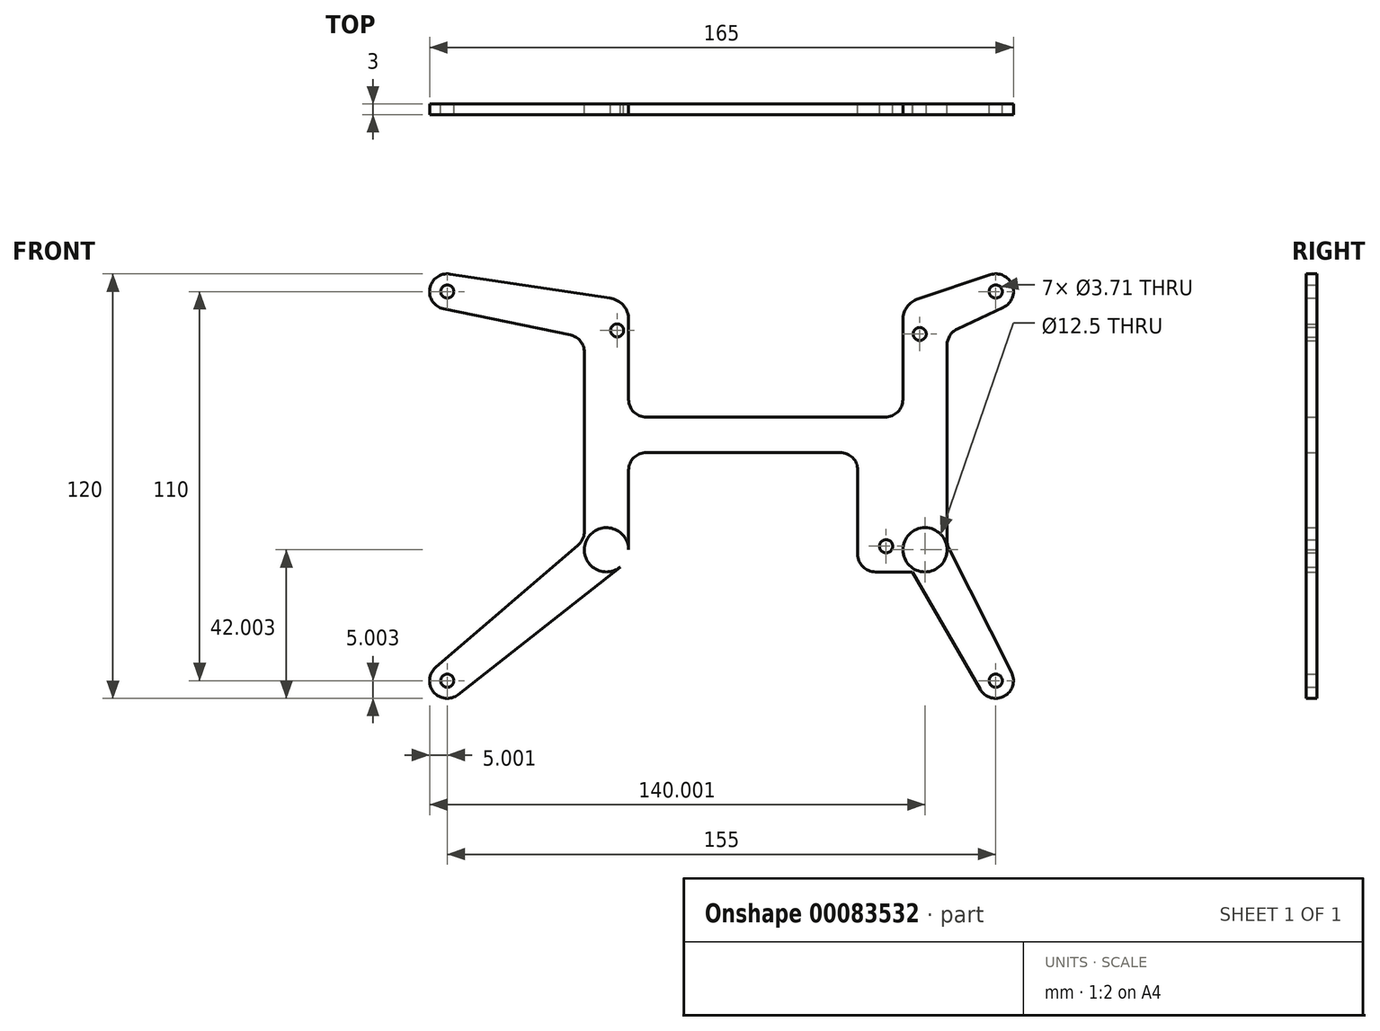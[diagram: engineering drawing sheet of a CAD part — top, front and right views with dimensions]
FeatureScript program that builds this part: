
annotation { "Feature Type Name" : "Feature", "Feature Type Description" : "" }
export const myFeature = defineFeature(function(context is Context, id is Id, definition is map)
    precondition{}
    {
        {
            var Q0;
            Q0=qCreatedBy(makeId("Front.planeOp"),FACE);
            var sketch = newSketch(context, id + "F0", { "sketchPlane" : qUnion([Q0])});
            skLineSegment(sketch, "E0.bottom", {"start": v(-70.99, 55.43) * mm, "end": v(84.01, 55.43) * mm});
            skLineSegment(sketch, "E0.top", {"start": v(-70.99, -54.57) * mm, "end": v(84.01, -54.57) * mm});
            skLineSegment(sketch, "E0.left", {"start": v(-70.99, 55.43) * mm, "end": v(-70.99, -54.57) * mm});
            skLineSegment(sketch, "E0.right", {"start": v(84.01, 55.43) * mm, "end": v(84.01, -54.57) * mm});
            skCircle(sketch, "E1", {"center": v(-70.99, 55.43) * mm, "radius": 5 * mm});
            skCircle(sketch, "E2", {"center": v(84.01, 55.43) * mm, "radius": 5 * mm});
            skCircle(sketch, "E3", {"center": v(84.01, -54.57) * mm, "radius": 5 * mm});
            skCircle(sketch, "E4", {"center": v(-70.99, -54.57) * mm, "radius": 5 * mm});
            skLineSegment(sketch, "E5", {"start": v(84.01, 55.43) * mm, "end": v(84.01, 47.43) * mm});
            skLineSegment(sketch, "E6", {"start": v(84.01, 47.43) * mm, "end": v(64.01, 47.43) * mm});
            skCircle(sketch, "E7", {"center": v(64.01, 47.43) * mm, "radius": 6.25 * mm});
            skLineSegment(sketch, "E8", {"start": v(64.01, 47.43) * mm, "end": v(64.01, -17.57) * mm});
            skCircle(sketch, "E9", {"center": v(64.01, -17.57) * mm, "radius": 6.25 * mm});
            skLineSegment(sketch, "E10", {"start": v(64.01, 47.43) * mm, "end": v(-19.74, 47.43) * mm});
            skLineSegment(sketch, "E11", {"start": v(-25.99, 47.43) * mm, "end": v(-25.99, -17.57) * mm});
            skLineSegment(sketch, "E12", {"start": v(-25.99, -17.57) * mm, "end": v(64.01, -17.57) * mm});
            skCircle(sketch, "E13", {"center": v(-25.99, 47.43) * mm, "radius": 6.25 * mm});
            skCircle(sketch, "E14", {"center": v(-25.99, -17.57) * mm, "radius": 6.25 * mm});
            skLineSegment(sketch, "E15", {"start": v(-70.25, 60.38) * mm, "end": v(-25.06, 53.61) * mm});
            skLineSegment(sketch, "E16", {"start": v(-36.23, 43.16) * mm, "end": v(-72, 50.54) * mm});
            skLineSegment(sketch, "E17", {"start": v(-74.25, -50.77) * mm, "end": v(-33.98, -16.2) * mm});
            skLineSegment(sketch, "E18", {"start": v(82.43, 60.18) * mm, "end": v(62.03, 53.36) * mm});
            skLineSegment(sketch, "E19", {"start": v(86.13, 50.9) * mm, "end": v(73.14, 44.81) * mm});
            skLineSegment(sketch, "E20", {"start": v(79.68, -57.07) * mm, "end": v(58.6, -20.7) * mm});
            skLineSegment(sketch, "E21", {"start": v(88.48, -52.32) * mm, "end": v(70.8, -17.14) * mm});
            skLineSegment(sketch, "E22", {"start": v(50.01, -23.82) * mm, "end": v(66.05, -23.82) * mm});
            skLineSegment(sketch, "E23", {"start": v(-32.24, 38.27) * mm, "end": v(-32.24, -12.4) * mm});
            skLineSegment(sketch, "E24", {"start": v(-25.99, 53.68) * mm, "end": v(-25.52, 53.68) * mm});
            skLineSegment(sketch, "E25", {"start": v(70.26, -14.9) * mm, "end": v(70.26, 40.28) * mm});
            skLineSegment(sketch, "E26", {"start": v(-19.74, 47.43) * mm, "end": v(-19.74, 24.93) * mm});
            skLineSegment(sketch, "E27", {"start": v(57.76, 47.43) * mm, "end": v(57.76, 24.93) * mm});
            skLineSegment(sketch, "E28", {"start": v(-25.99, 47.43) * mm, "end": v(-22.99, 47.43) * mm});
            skLineSegment(sketch, "E29", {"start": v(-22.99, 47.43) * mm, "end": v(-22.99, 44.43) * mm});
            skCircle(sketch, "E30", {"center": v(-22.99, 44.43) * mm, "radius": 1.85 * mm});
            skLineSegment(sketch, "E31", {"start": v(-25.99, -17.57) * mm, "end": v(-23.99, -17.57) * mm});
            skLineSegment(sketch, "E32", {"start": v(-23.99, -17.57) * mm, "end": v(-23.99, -15.57) * mm});
            skCircle(sketch, "E33", {"center": v(-23.99, -15.57) * mm, "radius": 1.85 * mm});
            skLineSegment(sketch, "E34", {"start": v(64.01, -17.57) * mm, "end": v(53.01, -17.57) * mm});
            skLineSegment(sketch, "E35", {"start": v(53.01, -17.57) * mm, "end": v(53.01, -16.57) * mm});
            skCircle(sketch, "E36", {"center": v(53.01, -16.57) * mm, "radius": 1.85 * mm});
            skLineSegment(sketch, "E37", {"start": v(64.01, 47.43) * mm, "end": v(64.01, 43.43) * mm});
            skLineSegment(sketch, "E38", {"start": v(64.01, 43.43) * mm, "end": v(62.51, 43.43) * mm});
            skCircle(sketch, "E39", {"center": v(62.51, 43.43) * mm, "radius": 1.85 * mm});
            skLineSegment(sketch, "E40.0", {"start": v(-14.74, 9.93) * mm, "end": v(40.01, 9.93) * mm});
            skLineSegment(sketch, "E41.0", {"start": v(-14.74, 19.93) * mm, "end": v(52.76, 19.93) * mm});
            skLineSegment(sketch, "E42.trimOffspring", {"start": v(-19.74, 4.93) * mm, "end": v(-19.74, -17.57) * mm});
            skPoint(sketch, "E43.visualSharp", {"position": v(-19.74, 19.93) * mm});
            skArc(sketch, "E43.filletArc", {"start": v(-19.74, 24.93) * mm, "mid": v(-18.27, 21.4) * mm, "end": v(-14.74, 19.93) * mm});
            skPoint(sketch, "E44.visualSharp", {"position": v(-19.74, 9.93) * mm});
            skArc(sketch, "E44.filletArc", {"start": v(-14.74, 9.93) * mm, "mid": v(-18.27, 8.47) * mm, "end": v(-19.74, 4.93) * mm});
            skPoint(sketch, "E45.visualSharp", {"position": v(57.76, 19.93) * mm});
            skArc(sketch, "E45.filletArc", {"start": v(52.76, 19.93) * mm, "mid": v(56.3, 21.4) * mm, "end": v(57.76, 24.93) * mm});
            skLineSegment(sketch, "E46", {"start": v(45.01, 4.93) * mm, "end": v(45.01, -18.82) * mm});
            skArc(sketch, "E47.filletArc", {"start": v(-32.24, 38.27) * mm, "mid": v(-33.36, 41.42) * mm, "end": v(-36.23, 43.16) * mm});
            skArc(sketch, "E48.filletArc", {"start": v(-33.98, -16.2) * mm, "mid": v(-32.7, -14.49) * mm, "end": v(-32.24, -12.4) * mm});
            skArc(sketch, "E49.filletArc", {"start": v(45.01, 4.93) * mm, "mid": v(43.55, 8.47) * mm, "end": v(40.01, 9.93) * mm});
            skArc(sketch, "E50.filletArc", {"start": v(45.01, -18.82) * mm, "mid": v(46.48, -22.35) * mm, "end": v(50.01, -23.82) * mm});
            skLineSegment(sketch, "E51", {"start": v(-67.9, -58.5) * mm, "end": v(-22.12, -22.48) * mm});
            skLineSegment(sketch, "E52.trimOffspring", {"start": v(63, 53.68) * mm, "end": v(64.01, 53.68) * mm});
            skCircle(sketch, "E53", {"center": v(-70.99, 55.43) * mm, "radius": 1.85 * mm});
            skCircle(sketch, "E54", {"center": v(-70.99, -54.57) * mm, "radius": 1.85 * mm});
            skCircle(sketch, "E55", {"center": v(84.01, -54.57) * mm, "radius": 1.85 * mm});
            skCircle(sketch, "E56", {"center": v(84.01, 55.43) * mm, "radius": 1.85 * mm});
            skArc(sketch, "E57.filletArc", {"start": v(73.14, 44.81) * mm, "mid": v(71.04, 42.97) * mm, "end": v(70.26, 40.28) * mm});
            skArc(sketch, "E58.filletArc", {"start": v(70.26, -14.9) * mm, "mid": v(70.4, -16.05) * mm, "end": v(70.8, -17.14) * mm});
            skSolve(sketch);
        }
        {
            var Q0;
            Q0=makeQuery(id+"F0.imprint","IMPRINT",FACE,{"disambiguationData":[TD([[makeQuery(id+"F0.imprint","IMPRINT",EDGE,{"derivedFrom":sQuery(id+"F0.wireOp",EDGE,"E23")}),1.0]])]});
            var Q1;
            {var subQ0=sQuery(id+"F0.wireOp",EDGE,"E15");var subQ1=sQuery(id+"F0.wireOp",EDGE,"E0.bottom");var subQ2=makeQuery(id+"F0.imprint","INTERSECT",VERTEX,{"derivedFrom":[subQ1,subQ0]});Q1=makeQuery(id+"F0.imprint","IMPRINT",FACE,{"disambiguationData":[TD([[makeQuery(id+"F0.imprint","IMPRINT",EDGE,{"disambiguationData":[TD([[subQ2,1.0]])],"derivedFrom":subQ1}),1.0]])]});}
            var Q2;
            Q2=makeQuery(id+"F0.imprint","IMPRINT",FACE,{"disambiguationData":[TD([[makeQuery(id+"F0.imprint","IMPRINT",EDGE,{"derivedFrom":sQuery(id+"F0.wireOp",EDGE,"E30")}),-1.0]])]});
            var Q3;
            {var subQ7=sQuery(id+"F0.wireOp",EDGE,"E26");Q3=makeQuery(id+"F0.imprint","IMPRINT",FACE,{"disambiguationData":[TD([[makeQuery(id+"F0.imprint","IMPRINT",EDGE,{"derivedFrom":subQ7}),-1.0]])]});}
            var Q4;
            {var subQ4=sQuery(id+"F0.wireOp",EDGE,"E31");Q4=makeQuery(id+"F0.imprint","IMPRINT",FACE,{"disambiguationData":[TD([[makeQuery(id+"F0.imprint","IMPRINT",EDGE,{"derivedFrom":subQ4}),-1.0]])]});}
            var Q5;
            {var subQ0=sQuery(id+"F0.wireOp",EDGE,"E31");Q5=makeQuery(id+"F0.imprint","IMPRINT",FACE,{"disambiguationData":[TD([[makeQuery(id+"F0.imprint","IMPRINT",EDGE,{"derivedFrom":subQ0}),1.0]])]});}
            var Q6;
            {var subQ0=sQuery(id+"F0.wireOp",EDGE,"E51");var subQ1=sQuery(id+"F0.wireOp",EDGE,"E0.top");var subQ2=makeQuery(id+"F0.imprint","INTERSECT",VERTEX,{"derivedFrom":[subQ1,subQ0]});Q6=makeQuery(id+"F0.imprint","IMPRINT",FACE,{"disambiguationData":[TD([[makeQuery(id+"F0.imprint","IMPRINT",EDGE,{"disambiguationData":[TD([[subQ2,1.0]])],"derivedFrom":subQ1}),-1.0]])]});}
            var Q7;
            {var subQ0=sQuery(id+"F0.wireOp",EDGE,"E17");var subQ1=sQuery(id+"F0.wireOp",EDGE,"E0.left");var subQ2=makeQuery(id+"F0.imprint","INTERSECT",VERTEX,{"derivedFrom":[subQ1,subQ0]});Q7=makeQuery(id+"F0.imprint","IMPRINT",FACE,{"disambiguationData":[TD([[makeQuery(id+"F0.imprint","IMPRINT",EDGE,{"disambiguationData":[TD([[subQ2,-1.0]])],"derivedFrom":subQ1}),-1.0]])]});}
            var Q8;
            {var subQ5=sQuery(id+"F0.wireOp",EDGE,"E50.filletArc");Q8=makeQuery(id+"F0.imprint","IMPRINT",FACE,{"disambiguationData":[TD([[makeQuery(id+"F0.imprint","IMPRINT",EDGE,{"derivedFrom":subQ5}),1.0]])]});}
            var Q9;
            {var subQ0=sQuery(id+"F0.wireOp",EDGE,"E7");var subQ1=makeQuery(id+"F0.imprint","INTERSECT",VERTEX,{"derivedFrom":[subQ0,sQuery(id+"F0.wireOp",EDGE,"E18")]});Q9=makeQuery(id+"F0.imprint","IMPRINT",FACE,{"disambiguationData":[TD([[makeQuery(id+"F0.imprint","IMPRINT",EDGE,{"disambiguationData":[TD([[subQ1,1.0]])],"derivedFrom":subQ0}),1.0]])]});}
            var Q10;
            {var subQ0=sQuery(id+"F0.wireOp",EDGE,"E18");var subQ1=sQuery(id+"F0.wireOp",EDGE,"E0.bottom");var subQ2=makeQuery(id+"F0.imprint","INTERSECT",VERTEX,{"derivedFrom":[subQ1,subQ0]});Q10=makeQuery(id+"F0.imprint","IMPRINT",FACE,{"disambiguationData":[TD([[makeQuery(id+"F0.imprint","IMPRINT",EDGE,{"disambiguationData":[TD([[subQ2,-1.0]])],"derivedFrom":subQ1}),1.0]])]});}
            var Q11;
            {var subQ1=sQuery(id+"F0.wireOp",EDGE,"E7");var subQ5=makeQuery(id+"F0.imprint","INTERSECT",VERTEX,{"derivedFrom":[subQ1,sQuery(id+"F0.wireOp",EDGE,"E19")]});Q11=makeQuery(id+"F0.imprint","IMPRINT",FACE,{"disambiguationData":[TD([[makeQuery(id+"F0.imprint","IMPRINT",EDGE,{"disambiguationData":[TD([[subQ5,1.0]])],"derivedFrom":subQ1}),1.0]])]});}
            var Q12;
            {var subQ11=sQuery(id+"F0.wireOp",EDGE,"E52.trimOffspring");Q12=makeQuery(id+"F0.imprint","IMPRINT",FACE,{"disambiguationData":[TD([[makeQuery(id+"F0.imprint","IMPRINT",EDGE,{"derivedFrom":subQ11}),1.0]])]});}
            var Q13;
            {var subQ1=sQuery(id+"F0.wireOp",EDGE,"E6");var subQ3=sQuery(id+"F0.wireOp",EDGE,"E19");var subQ4=makeQuery(id+"F0.imprint","INTERSECT",VERTEX,{"derivedFrom":[subQ1,subQ3]});Q13=makeQuery(id+"F0.imprint","IMPRINT",FACE,{"disambiguationData":[TD([[makeQuery(id+"F0.imprint","IMPRINT",EDGE,{"disambiguationData":[TD([[subQ4,-1.0]])],"derivedFrom":subQ3}),-1.0]])]});}
            var Q14;
            {var subQ0=sQuery(id+"F0.wireOp",EDGE,"E19");var subQ1=sQuery(id+"F0.wireOp",EDGE,"E7");var subQ2=makeQuery(id+"F0.imprint","INTERSECT",VERTEX,{"derivedFrom":[subQ1,subQ0]});Q14=makeQuery(id+"F0.imprint","IMPRINT",FACE,{"disambiguationData":[TD([[makeQuery(id+"F0.imprint","IMPRINT",EDGE,{"disambiguationData":[TD([[subQ2,1.0]])],"derivedFrom":subQ0}),-1.0]])]});}
            var Q15;
            {var subQ3=sQuery(id+"F0.wireOp",EDGE,"E7");var subQ7=sQuery(id+"F0.wireOp",EDGE,"E8");var subQ8=makeQuery(id+"F0.imprint","INTERSECT",VERTEX,{"derivedFrom":[subQ3,subQ7]});Q15=makeQuery(id+"F0.imprint","IMPRINT",FACE,{"disambiguationData":[TD([[makeQuery(id+"F0.imprint","IMPRINT",EDGE,{"disambiguationData":[TD([[subQ8,1.0]])],"derivedFrom":subQ7}),-1.0]])]});}
            var Q16;
            {var subQ0=sQuery(id+"F0.wireOp",EDGE,"E34");var subQ1=sQuery(id+"F0.wireOp",EDGE,"E8");var subQ2=makeQuery(id+"F0.imprint","INTERSECT",VERTEX,{"derivedFrom":[subQ1,subQ0]});Q16=makeQuery(id+"F0.imprint","IMPRINT",FACE,{"disambiguationData":[TD([[makeQuery(id+"F0.imprint","IMPRINT",EDGE,{"disambiguationData":[TD([[subQ2,1.0]])],"derivedFrom":subQ1}),-1.0]])]});}
            var Q17;
            {var subQ2=sQuery(id+"F0.wireOp",EDGE,"E34");var subQ5=sQuery(id+"F0.wireOp",EDGE,"E8");var subQ7=makeQuery(id+"F0.imprint","INTERSECT",VERTEX,{"derivedFrom":[subQ5,subQ2]});Q17=makeQuery(id+"F0.imprint","IMPRINT",FACE,{"disambiguationData":[TD([[makeQuery(id+"F0.imprint","IMPRINT",EDGE,{"disambiguationData":[TD([[subQ7,1.0]])],"derivedFrom":subQ5}),1.0]])]});}
            var Q18;
            {var subQ0=sQuery(id+"F0.wireOp",EDGE,"E20");var subQ1=sQuery(id+"F0.wireOp",EDGE,"E9");var subQ2=makeQuery(id+"F0.imprint","INTERSECT",VERTEX,{"derivedFrom":[subQ1,subQ0]});Q18=makeQuery(id+"F0.imprint","IMPRINT",FACE,{"disambiguationData":[TD([[makeQuery(id+"F0.imprint","IMPRINT",EDGE,{"disambiguationData":[TD([[subQ2,-1.0]])],"derivedFrom":subQ1}),-1.0]])]});}
            var Q19;
            {var subQ1=sQuery(id+"F0.wireOp",EDGE,"E0.top");var subQ13=sQuery(id+"F0.wireOp",EDGE,"E20");var subQ14=makeQuery(id+"F0.imprint","INTERSECT",VERTEX,{"derivedFrom":[subQ1,subQ13]});Q19=makeQuery(id+"F0.imprint","IMPRINT",FACE,{"disambiguationData":[TD([[makeQuery(id+"F0.imprint","IMPRINT",EDGE,{"disambiguationData":[TD([[subQ14,-1.0]])],"derivedFrom":subQ1}),1.0]])]});}
            var Q20;
            {var subQ0=sQuery(id+"F0.wireOp",EDGE,"E21");var subQ1=sQuery(id+"F0.wireOp",EDGE,"E0.right");var subQ2=makeQuery(id+"F0.imprint","INTERSECT",VERTEX,{"derivedFrom":[subQ1,subQ0]});Q20=makeQuery(id+"F0.imprint","IMPRINT",FACE,{"disambiguationData":[TD([[makeQuery(id+"F0.imprint","IMPRINT",EDGE,{"disambiguationData":[TD([[subQ2,-1.0]])],"derivedFrom":subQ1}),1.0]])]});}
            var Q21;
            {var subQ3=sQuery(id+"F0.wireOp",EDGE,"E53");var subQ7=sQuery(id+"F0.wireOp",EDGE,"E0.bottom");var subQ9=makeQuery(id+"F0.imprint","INTERSECT",VERTEX,{"derivedFrom":[subQ7,subQ3]});Q21=makeQuery(id+"F0.imprint","IMPRINT",FACE,{"disambiguationData":[TD([[makeQuery(id+"F0.imprint","IMPRINT",EDGE,{"disambiguationData":[TD([[subQ9,-1.0]])],"derivedFrom":subQ7}),1.0]])]});}
            var Q22;
            {var subQ0=sQuery(id+"F0.wireOp",EDGE,"E53");var subQ1=sQuery(id+"F0.wireOp",EDGE,"E0.bottom");var subQ2=makeQuery(id+"F0.imprint","INTERSECT",VERTEX,{"derivedFrom":[subQ1,subQ0]});Q22=makeQuery(id+"F0.imprint","IMPRINT",FACE,{"disambiguationData":[TD([[makeQuery(id+"F0.imprint","IMPRINT",EDGE,{"disambiguationData":[TD([[subQ2,-1.0]])],"derivedFrom":subQ1}),-1.0]])]});}
            var Q23;
            {var subQ0=sQuery(id+"F0.wireOp",EDGE,"E2");var subQ5=sQuery(id+"F0.wireOp",EDGE,"E0.bottom");var subQ6=makeQuery(id+"F0.imprint","INTERSECT",VERTEX,{"derivedFrom":[subQ5,subQ0]});Q23=makeQuery(id+"F0.imprint","IMPRINT",FACE,{"disambiguationData":[TD([[makeQuery(id+"F0.imprint","IMPRINT",EDGE,{"disambiguationData":[TD([[subQ6,-1.0]])],"derivedFrom":subQ5}),1.0]])]});}
            var Q24;
            {var subQ0=sQuery(id+"F0.wireOp",EDGE,"E2");var subQ1=sQuery(id+"F0.wireOp",EDGE,"E0.bottom");var subQ2=makeQuery(id+"F0.imprint","INTERSECT",VERTEX,{"derivedFrom":[subQ1,subQ0]});Q24=makeQuery(id+"F0.imprint","IMPRINT",FACE,{"disambiguationData":[TD([[makeQuery(id+"F0.imprint","IMPRINT",EDGE,{"disambiguationData":[TD([[subQ2,-1.0]])],"derivedFrom":subQ1}),-1.0]])]});}
            var Q25;
            {var subQ0=sQuery(id+"F0.wireOp",EDGE,"E54");var subQ1=sQuery(id+"F0.wireOp",EDGE,"E0.top");var subQ2=makeQuery(id+"F0.imprint","INTERSECT",VERTEX,{"derivedFrom":[subQ1,subQ0]});Q25=makeQuery(id+"F0.imprint","IMPRINT",FACE,{"disambiguationData":[TD([[makeQuery(id+"F0.imprint","IMPRINT",EDGE,{"disambiguationData":[TD([[subQ2,-1.0]])],"derivedFrom":subQ1}),1.0]])]});}
            var Q26;
            {var subQ5=sQuery(id+"F0.wireOp",EDGE,"E54");var subQ7=sQuery(id+"F0.wireOp",EDGE,"E0.top");var subQ8=makeQuery(id+"F0.imprint","INTERSECT",VERTEX,{"derivedFrom":[subQ7,subQ5]});Q26=makeQuery(id+"F0.imprint","IMPRINT",FACE,{"disambiguationData":[TD([[makeQuery(id+"F0.imprint","IMPRINT",EDGE,{"disambiguationData":[TD([[subQ8,-1.0]])],"derivedFrom":subQ7}),-1.0]])]});}
            var Q27;
            {var subQ0=sQuery(id+"F0.wireOp",EDGE,"E3");var subQ1=sQuery(id+"F0.wireOp",EDGE,"E0.top");var subQ2=makeQuery(id+"F0.imprint","INTERSECT",VERTEX,{"derivedFrom":[subQ1,subQ0]});Q27=makeQuery(id+"F0.imprint","IMPRINT",FACE,{"disambiguationData":[TD([[makeQuery(id+"F0.imprint","IMPRINT",EDGE,{"disambiguationData":[TD([[subQ2,-1.0]])],"derivedFrom":subQ1}),1.0]])]});}
            var Q28;
            {var subQ0=sQuery(id+"F0.wireOp",EDGE,"E3");var subQ2=sQuery(id+"F0.wireOp",EDGE,"E0.top");var subQ3=makeQuery(id+"F0.imprint","INTERSECT",VERTEX,{"derivedFrom":[subQ2,subQ0]});Q28=makeQuery(id+"F0.imprint","IMPRINT",FACE,{"disambiguationData":[TD([[makeQuery(id+"F0.imprint","IMPRINT",EDGE,{"disambiguationData":[TD([[subQ3,-1.0]])],"derivedFrom":subQ2}),-1.0]])]});}
            var Q29;
            {var subQ0=sQuery(id+"F0.wireOp",EDGE,"E20");var subQ1=sQuery(id+"F0.wireOp",EDGE,"E0.top");var subQ2=makeQuery(id+"F0.imprint","INTERSECT",VERTEX,{"derivedFrom":[subQ1,subQ0]});Q29=makeQuery(id+"F0.imprint","IMPRINT",FACE,{"disambiguationData":[TD([[makeQuery(id+"F0.imprint","IMPRINT",EDGE,{"disambiguationData":[TD([[subQ2,-1.0]])],"derivedFrom":subQ1}),-1.0]])]});}
            var Q30;
            {var subQ0=sQuery(id+"F0.wireOp",EDGE,"E21");var subQ1=sQuery(id+"F0.wireOp",EDGE,"E9");var subQ2=makeQuery(id+"F0.imprint","INTERSECT",VERTEX,{"derivedFrom":[subQ1,subQ0]});Q30=makeQuery(id+"F0.imprint","IMPRINT",FACE,{"disambiguationData":[TD([[makeQuery(id+"F0.imprint","IMPRINT",EDGE,{"disambiguationData":[TD([[subQ2,1.0]])],"derivedFrom":subQ1}),-1.0]])]});}
            var Q31;
            {var subQ0=sQuery(id+"F0.wireOp",EDGE,"E19");var subQ1=sQuery(id+"F0.wireOp",EDGE,"E2");var subQ2=makeQuery(id+"F0.imprint","INTERSECT",VERTEX,{"derivedFrom":[subQ1,subQ0]});Q31=makeQuery(id+"F0.imprint","IMPRINT",FACE,{"disambiguationData":[TD([[makeQuery(id+"F0.imprint","IMPRINT",EDGE,{"disambiguationData":[TD([[subQ2,1.0]])],"derivedFrom":subQ1}),-1.0]])]});}
            var Q32;
            {var subQ3=sQuery(id+"F0.wireOp",EDGE,"E52.trimOffspring");Q32=makeQuery(id+"F0.imprint","IMPRINT",FACE,{"disambiguationData":[TD([[makeQuery(id+"F0.imprint","IMPRINT",EDGE,{"derivedFrom":subQ3}),-1.0]])]});}
            var Q33;
            {var subQ0=sQuery(id+"F0.wireOp",EDGE,"E16");var subQ1=sQuery(id+"F0.wireOp",EDGE,"E0.left");var subQ2=makeQuery(id+"F0.imprint","INTERSECT",VERTEX,{"derivedFrom":[subQ1,subQ0]});Q33=makeQuery(id+"F0.imprint","IMPRINT",FACE,{"disambiguationData":[TD([[makeQuery(id+"F0.imprint","IMPRINT",EDGE,{"disambiguationData":[TD([[subQ2,1.0]])],"derivedFrom":subQ1}),-1.0]])]});}
            var Q34;
            {var subQ3=sQuery(id+"F0.wireOp",EDGE,"E24");Q34=makeQuery(id+"F0.imprint","IMPRINT",FACE,{"disambiguationData":[TD([[makeQuery(id+"F0.imprint","IMPRINT",EDGE,{"derivedFrom":subQ3}),-1.0]])]});}
            var Q35;
            {var subQ0=sQuery(id+"F0.wireOp",EDGE,"E19");var subQ1=sQuery(id+"F0.wireOp",EDGE,"E7");var subQ2=makeQuery(id+"F0.imprint","INTERSECT",VERTEX,{"derivedFrom":[subQ1,subQ0]});Q35=makeQuery(id+"F0.imprint","IMPRINT",FACE,{"disambiguationData":[TD([[makeQuery(id+"F0.imprint","IMPRINT",EDGE,{"disambiguationData":[TD([[subQ2,1.0]])],"derivedFrom":subQ1}),-1.0]])]});}
            var Q36;
            {var subQ1=sQuery(id+"F0.wireOp",EDGE,"E7");var subQ6=sQuery(id+"F0.wireOp",EDGE,"E6");var subQ9=makeQuery(id+"F0.imprint","INTERSECT",VERTEX,{"derivedFrom":[subQ6,subQ1]});Q36=makeQuery(id+"F0.imprint","IMPRINT",FACE,{"disambiguationData":[TD([[makeQuery(id+"F0.imprint","IMPRINT",EDGE,{"disambiguationData":[TD([[subQ9,1.0]])],"derivedFrom":subQ1}),1.0]])]});}
            extrude(context, id + "F1", {"entities" : qUnion([Q0, Q1, Q2, Q3, Q4, Q5, Q6, Q7, Q8, Q9, Q10, Q11, Q12, Q13, Q14, Q15, Q16, Q17, Q18, Q19, Q20, Q21, Q22, Q23, Q24, Q25, Q26, Q27, Q28, Q29, Q30, Q31, Q32, Q33, Q34, Q35, Q36]), "depth" : 3 * mm});
        }
    });
